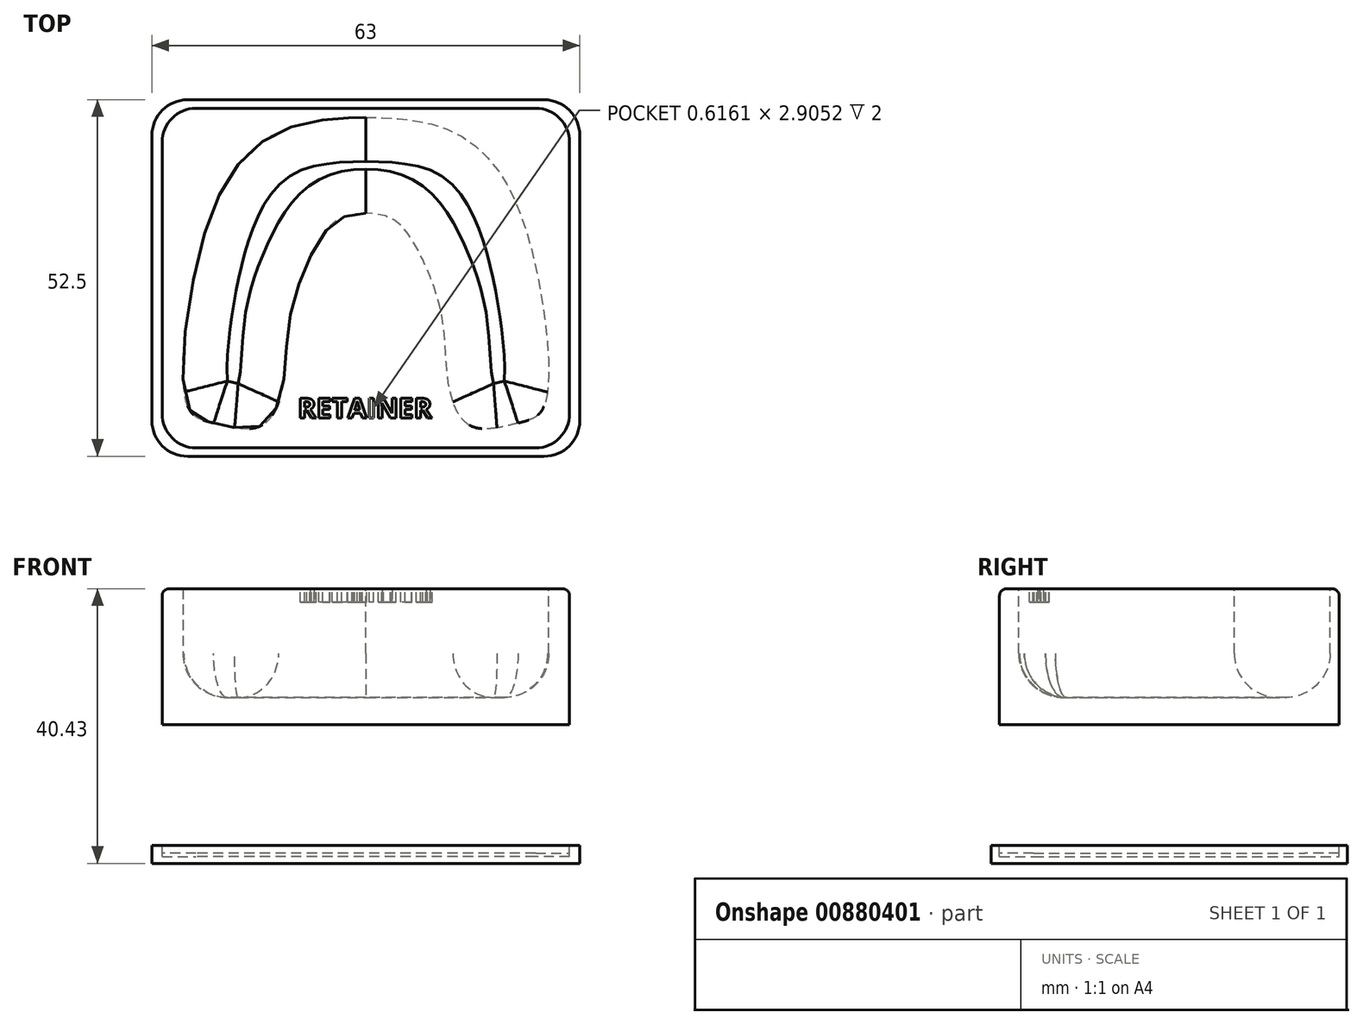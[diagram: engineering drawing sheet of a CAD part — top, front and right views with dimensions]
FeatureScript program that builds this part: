
annotation { "Feature Type Name" : "Feature", "Feature Type Description" : "" }
export const myFeature = defineFeature(function(context is Context, id is Id, definition is map)
    precondition{}
    {
        {
            var Q0;
            Q0=qCreatedBy(makeId("Top.planeOp"),FACE);
            var sketch = newSketch(context, id + "F0", { "sketchPlane" : qUnion([Q0])});
            skLineSegment(sketch, "E0.bottom", {"start": v(30, -25) * mm, "end": v(-30, -25) * mm});
            skLineSegment(sketch, "E0.top", {"start": v(30, 25) * mm, "end": v(-30, 25) * mm});
            skLineSegment(sketch, "E0.left", {"start": v(30, -25) * mm, "end": v(30, 25) * mm});
            skLineSegment(sketch, "E0.right", {"start": v(-30, -25) * mm, "end": v(-30, 25) * mm});
            skPoint(sketch, "E0.middle", {"position": v(0, 0) * mm});
            skSolve(sketch);
        }
        {
            var Q0;
            Q0=makeQuery(id+"F0.imprint","IMPRINT",FACE,{"disambiguationData":[TD([[makeQuery(id+"F0.imprint","IMPRINT",EDGE,{"derivedFrom":sQuery(id+"F0.wireOp",EDGE,"E0.bottom")}),-1.0]])]});
            extrude(context, id + "F1", {"entities" : qUnion([Q0]), "depth" : 20 * mm, "offsetDistance" : 25 * mm});
        }
        {
            var Q0;
            Q0=makeQuery(id+"F1.opExtrude","CAP_FACE",FACE,{"disambiguationData":[OSD([sQuery(id+"F0.wireOp",EDGE,"E0.bottom"),sQuery(id+"F0.wireOp",EDGE,"E0.top"),sQuery(id+"F0.wireOp",EDGE,"E0.left"),sQuery(id+"F0.wireOp",EDGE,"E0.right")])],"isStart":false});
            var sketch = newSketch(context, id + "F2", { "sketchPlane" : qUnion([Q0])});
            skFitSpline(sketch, "E1", {"points": [v(0, 23.67) * mm, v(3.13, 23.58) * mm, v(11.52, 22.1) * mm, v(19.52, 15.77) * mm, v(25.35, 0) * mm, v(26.14, -19.1) * mm, v(22.39, -21.36) * mm, v(15.67, -21.86) * mm, v(12.31, -16.33) * mm, v(11.33, -6.45) * mm, v(8.36, 2.74) * mm, v(4.31, 8.46) * mm, v(0, 9.55) * mm], "startDerivative": vector(53.03, -0.78) * mm, "endDerivative": vector(-77.74, 3.12) * mm});
            skFitSpline(sketch, "E2.MirrorCS", {"points": [v(0, 23.67) * mm, v(-3.13, 23.58) * mm, v(-11.52, 22.1) * mm, v(-19.52, 15.77) * mm, v(-25.35, 0) * mm, v(-26.14, -19.1) * mm, v(-22.39, -21.36) * mm, v(-15.67, -21.86) * mm, v(-12.31, -16.33) * mm, v(-11.33, -6.45) * mm, v(-8.36, 2.74) * mm, v(-4.31, 8.46) * mm, v(0, 9.55) * mm], "startDerivative": vector(-53.03, -0.78) * mm, "endDerivative": vector(77.74, 3.12) * mm});
            skSolve(sketch);
        }
        {
            var Q0;
            Q0=makeQuery(id+"F2.imprint","IMPRINT",FACE,{"disambiguationData":[TD([[makeQuery(id+"F2.imprint","IMPRINT",EDGE,{"derivedFrom":sQuery(id+"F2.wireOp",EDGE,"E1")}),-1.0]])]});
            extrude(context, id + "F3", {"entities" : qUnion([Q0]), "operationType" : NewBodyOperationType.REMOVE, "oppositeDirection" : true, "depth" : 16 * mm, "offsetDistance" : 25 * mm});
        }
        {
            var Q0;
            Q0=makeQuery(id+"F3.boolean.opBoolean","COPY",EDGE,{"derivedFrom":makeQuery(id+"F3.opExtrude","CAP_EDGE",EDGE,{"disambiguationData":[OSD([sQuery(id+"F2.wireOp",EDGE,"E2.MirrorCS")])],"isStart":false})});
            var Q1;
            Q1=makeQuery(id+"F3.boolean.opBoolean","COPY",EDGE,{"derivedFrom":makeQuery(id+"F3.opExtrude","CAP_EDGE",EDGE,{"disambiguationData":[OSD([sQuery(id+"F2.wireOp",EDGE,"E1")])],"isStart":false})});
            var Q2;
            Q2=makeQuery(id+"F3.boolean.opBoolean","COPY",FACE,{"derivedFrom":makeQuery(id+"F3.opExtrude","CAP_FACE",FACE,{"disambiguationData":[OSD([sQuery(id+"F2.wireOp",EDGE,"E1"),sQuery(id+"F2.wireOp",EDGE,"E2.MirrorCS")])],"isStart":false})});
            fillet(context, id + "F4", {"entities" : qUnion([Q0, Q1, Q2]), "radius" : 6.5 * mm, "tangentPropagation" : true, "allowEdgeOverflow" : false});
        }
        {
            var Q0;
            Q0=makeQuery(id+"F1.opExtrude","SWEPT_EDGE",EDGE,{"disambiguationData":[OSD([sQuery(id+"F0.wireOp",EDGE,"E0.top"),sQuery(id+"F0.wireOp",EDGE,"E0.right")])]});
            var Q1;
            Q1=makeQuery(id+"F1.opExtrude","SWEPT_EDGE",EDGE,{"disambiguationData":[OSD([sQuery(id+"F0.wireOp",EDGE,"E0.bottom"),sQuery(id+"F0.wireOp",EDGE,"E0.right")])]});
            var Q2;
            Q2=makeQuery(id+"F1.opExtrude","SWEPT_EDGE",EDGE,{"disambiguationData":[OSD([sQuery(id+"F0.wireOp",EDGE,"E0.bottom"),sQuery(id+"F0.wireOp",EDGE,"E0.left")])]});
            var Q3;
            Q3=makeQuery(id+"F1.opExtrude","SWEPT_EDGE",EDGE,{"disambiguationData":[OSD([sQuery(id+"F0.wireOp",EDGE,"E0.top"),sQuery(id+"F0.wireOp",EDGE,"E0.left")])]});
            fillet(context, id + "F5", {"entities" : qUnion([Q0, Q1, Q2, Q3]), "radius" : 5 * mm, "tangentPropagation" : true, "allowEdgeOverflow" : false});
        }
        {
            var Q0;
            Q0=makeQuery(id+"F3.boolean.opBoolean","COPY",EDGE,{"derivedFrom":makeQuery(id+"F3.opExtrude","CAP_EDGE",EDGE,{"disambiguationData":[OSD([sQuery(id+"F2.wireOp",EDGE,"E2.MirrorCS")])],"isStart":true})});
            var Q1;
            Q1=makeQuery(id+"F3.boolean.opBoolean","COPY",EDGE,{"derivedFrom":makeQuery(id+"F3.opExtrude","CAP_EDGE",EDGE,{"disambiguationData":[OSD([sQuery(id+"F2.wireOp",EDGE,"E1")])],"isStart":true})});
            var Q2;
            Q2=makeQuery(id+"F1.opExtrude","CAP_EDGE",EDGE,{"disambiguationData":[OSD([sQuery(id+"F0.wireOp",EDGE,"E0.top")])],"isStart":false});
            fillet(context, id + "F6", {"entities" : qUnion([Q0, Q1, Q2]), "radius" : 1 * mm, "tangentPropagation" : true, "allowEdgeOverflow" : false});
        }
        {
            var Q0;
            Q0=makeQuery(id+"F1.opExtrude","CAP_FACE",FACE,{"disambiguationData":[OSD([sQuery(id+"F0.wireOp",EDGE,"E0.bottom"),sQuery(id+"F0.wireOp",EDGE,"E0.top"),sQuery(id+"F0.wireOp",EDGE,"E0.left"),sQuery(id+"F0.wireOp",EDGE,"E0.right")])],"isStart":true});
            extrude(context, id + "F7", {"entities" : qUnion([Q0]), "depth" : 2.5 * mm, "offsetDistance" : 25 * mm});
        }
        {
            var Q0;
            Q0=qCreatedBy(makeId("Front.planeOp"),FACE);
            var sketch = newSketch(context, id + "F8", { "sketchPlane" : qUnion([Q0])});
            skLineSegment(sketch, "E3", {"start": v(0, 0) * mm, "end": v(0, -16.95) * mm});
            skSolve(sketch);
        }
        {
            var Q0;
            Q0=makeQuery(id+"F7.opExtrude","SWEPT_BODY",BODY,{"disambiguationData":[OSD([sQuery(id+"F0.wireOp",EDGE,"E0.bottom"),sQuery(id+"F0.wireOp",EDGE,"E0.top"),sQuery(id+"F0.wireOp",EDGE,"E0.left"),sQuery(id+"F0.wireOp",EDGE,"E0.right")])]});
            var Q1;
            Q1=sQuery(id+"F8.wireOp",EDGE,"E3");
            transform(context, id + "F9", {"entities" : qUnion([Q0]), "transformType" : TransformType.TRANSLATION_ENTITY, "oppositeDirectionEntity" : false, "transformLine" : qUnion([Q1]), "makeCopy" : false});
        }
        {
            var Q0;
            Q0=makeQuery(id+"F7.opExtrude","SWEPT_BODY",BODY,{"disambiguationData":[OSD([sQuery(id+"F0.wireOp",EDGE,"E0.bottom"),sQuery(id+"F0.wireOp",EDGE,"E0.top"),sQuery(id+"F0.wireOp",EDGE,"E0.left"),sQuery(id+"F0.wireOp",EDGE,"E0.right")])]});
            var Q1;
            Q1=qCreatedBy(makeId("Origin.pointOp"),VERTEX);
            transform(context, id + "F10", {"entities" : qUnion([Q0]), "transformType" : TransformType.SCALE_UNIFORMLY, "scale" : 1.05, "scalePoint" : qUnion([Q1]), "makeCopy" : true});
        }
        {
            var Q0;
            Q0=makeQuery(id+"F7.opExtrude","CAP_FACE",FACE,{"disambiguationData":[OSD([sQuery(id+"F0.wireOp",EDGE,"E0.bottom"),sQuery(id+"F0.wireOp",EDGE,"E0.top"),sQuery(id+"F0.wireOp",EDGE,"E0.left"),sQuery(id+"F0.wireOp",EDGE,"E0.right")])],"isStart":true});
            extrude(context, id + "F11", {"entities" : qUnion([Q0]), "operationType" : NewBodyOperationType.REMOVE, "oppositeDirection" : true, "depth" : 2 * mm, "offsetDistance" : 25 * mm});
        }
        {
            var Q0;
            Q0=makeQuery(id+"F1.opExtrude","CAP_FACE",FACE,{"disambiguationData":[OSD([sQuery(id+"F0.wireOp",EDGE,"E0.bottom"),sQuery(id+"F0.wireOp",EDGE,"E0.top"),sQuery(id+"F0.wireOp",EDGE,"E0.left"),sQuery(id+"F0.wireOp",EDGE,"E0.right")])],"isStart":false});
            var sketch = newSketch(context, id + "F12", { "sketchPlane" : qUnion([Q0])});
            skText(sketch, "E4", { "text": "RETAINER", "fontName": "OpenSans-Bold.ttf"});
            const initialGuessF12  = {"E4": [-0.01, -0.02061, 1, 0, 0.00293]};
            skSetInitialGuess(sketch, initialGuessF12);
            skSolve(sketch);
        }
        {
            var Q0;
            Q0 = qSketchRegion(id + "F12", true);
            extrude(context, id + "F13", {"entities" : qUnion([Q0]), "operationType" : NewBodyOperationType.REMOVE, "oppositeDirection" : true, "depth" : 2 * mm, "offsetDistance" : 25 * mm});
        }
    });
